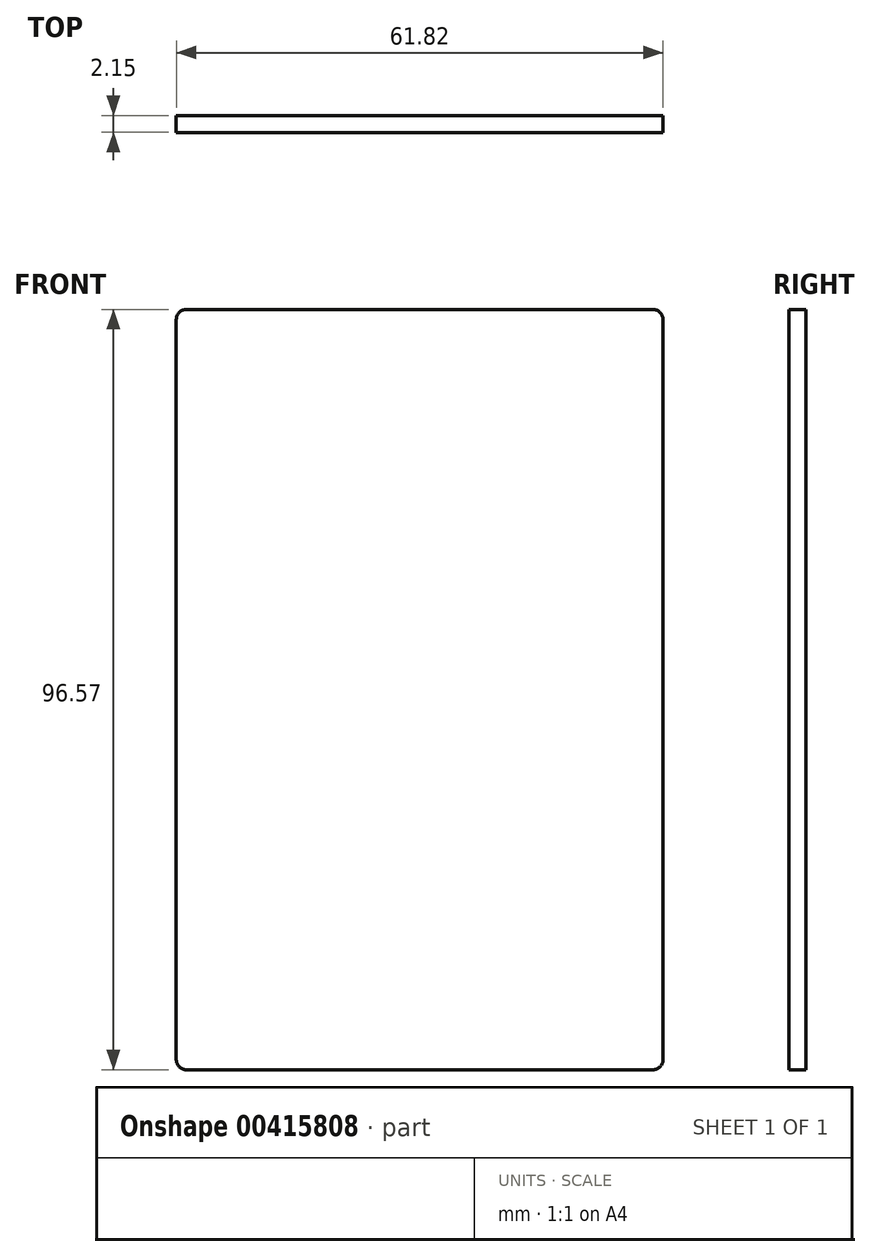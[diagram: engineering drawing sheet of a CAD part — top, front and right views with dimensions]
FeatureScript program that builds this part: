
annotation { "Feature Type Name" : "Feature", "Feature Type Description" : "" }
export const myFeature = defineFeature(function(context is Context, id is Id, definition is map)
    precondition{}
    {
        {
            var Q0;
            Q0=qCreatedBy(makeId("Front.planeOp"),FACE);
            var sketch = newSketch(context, id + "F0", { "sketchPlane" : qUnion([Q0])});
            skLineSegment(sketch, "E0.bottom", {"start": v(-36.86, 50.13) * mm, "end": v(24.96, 50.13) * mm});
            skLineSegment(sketch, "E0.top", {"start": v(-36.86, -46.44) * mm, "end": v(24.96, -46.44) * mm});
            skLineSegment(sketch, "E0.left", {"start": v(-36.86, 50.13) * mm, "end": v(-36.86, -46.44) * mm});
            skLineSegment(sketch, "E0.right", {"start": v(24.96, 50.13) * mm, "end": v(24.96, -46.44) * mm});
            skSolve(sketch);
        }
        {
            var Q0;
            Q0 = qSketchRegion(id + "F0", true);
            extrude(context, id + "F1", {"entities" : qUnion([Q0]), "depth" : 1.27 * mm});
        }
        {
            var Q0;
            Q0=makeQuery(id+"F1.opExtrude","SWEPT_EDGE",EDGE,{"disambiguationData":[OSD([sQuery(id+"F0.wireOp",EDGE,"E0.top"),sQuery(id+"F0.wireOp",EDGE,"E0.left")])]});
            fillet(context, id + "F2", {"entities" : qUnion([Q0]), "radius" : 1.27 * mm, "tangentPropagation" : true, "allowEdgeOverflow" : false});
        }
        {
            var Q0;
            Q0=makeQuery(id+"F1.opExtrude","SWEPT_EDGE",EDGE,{"disambiguationData":[OSD([sQuery(id+"F0.wireOp",EDGE,"E0.top"),sQuery(id+"F0.wireOp",EDGE,"E0.right")])]});
            fillet(context, id + "F3", {"entities" : qUnion([Q0]), "radius" : 1.27 * mm, "tangentPropagation" : true, "allowEdgeOverflow" : false});
        }
        {
            var Q0;
            Q0=makeQuery(id+"F1.opExtrude","SWEPT_EDGE",EDGE,{"disambiguationData":[OSD([sQuery(id+"F0.wireOp",EDGE,"E0.bottom"),sQuery(id+"F0.wireOp",EDGE,"E0.right")])]});
            fillet(context, id + "F4", {"entities" : qUnion([Q0]), "radius" : 1.27 * mm, "tangentPropagation" : true, "allowEdgeOverflow" : false});
        }
        {
            var Q0;
            Q0=makeQuery(id+"F1.opExtrude","SWEPT_EDGE",EDGE,{"disambiguationData":[OSD([sQuery(id+"F0.wireOp",EDGE,"E0.bottom"),sQuery(id+"F0.wireOp",EDGE,"E0.left")])]});
            fillet(context, id + "F5", {"entities" : qUnion([Q0]), "radius" : 1.27 * mm, "tangentPropagation" : true, "allowEdgeOverflow" : false});
        }
        {
            var Q0;
            Q0=makeQuery(id+"F1.opExtrude","CAP_FACE",FACE,{"disambiguationData":[OSD([sQuery(id+"F0.wireOp",EDGE,"E0.bottom"),sQuery(id+"F0.wireOp",EDGE,"E0.top"),sQuery(id+"F0.wireOp",EDGE,"E0.left"),sQuery(id+"F0.wireOp",EDGE,"E0.right")])],"isStart":false});
            extrude(context, id + "F6", {"entities" : qUnion([Q0]), "operationType" : NewBodyOperationType.ADD, "depth" : 0.88 * mm});
        }
    });
